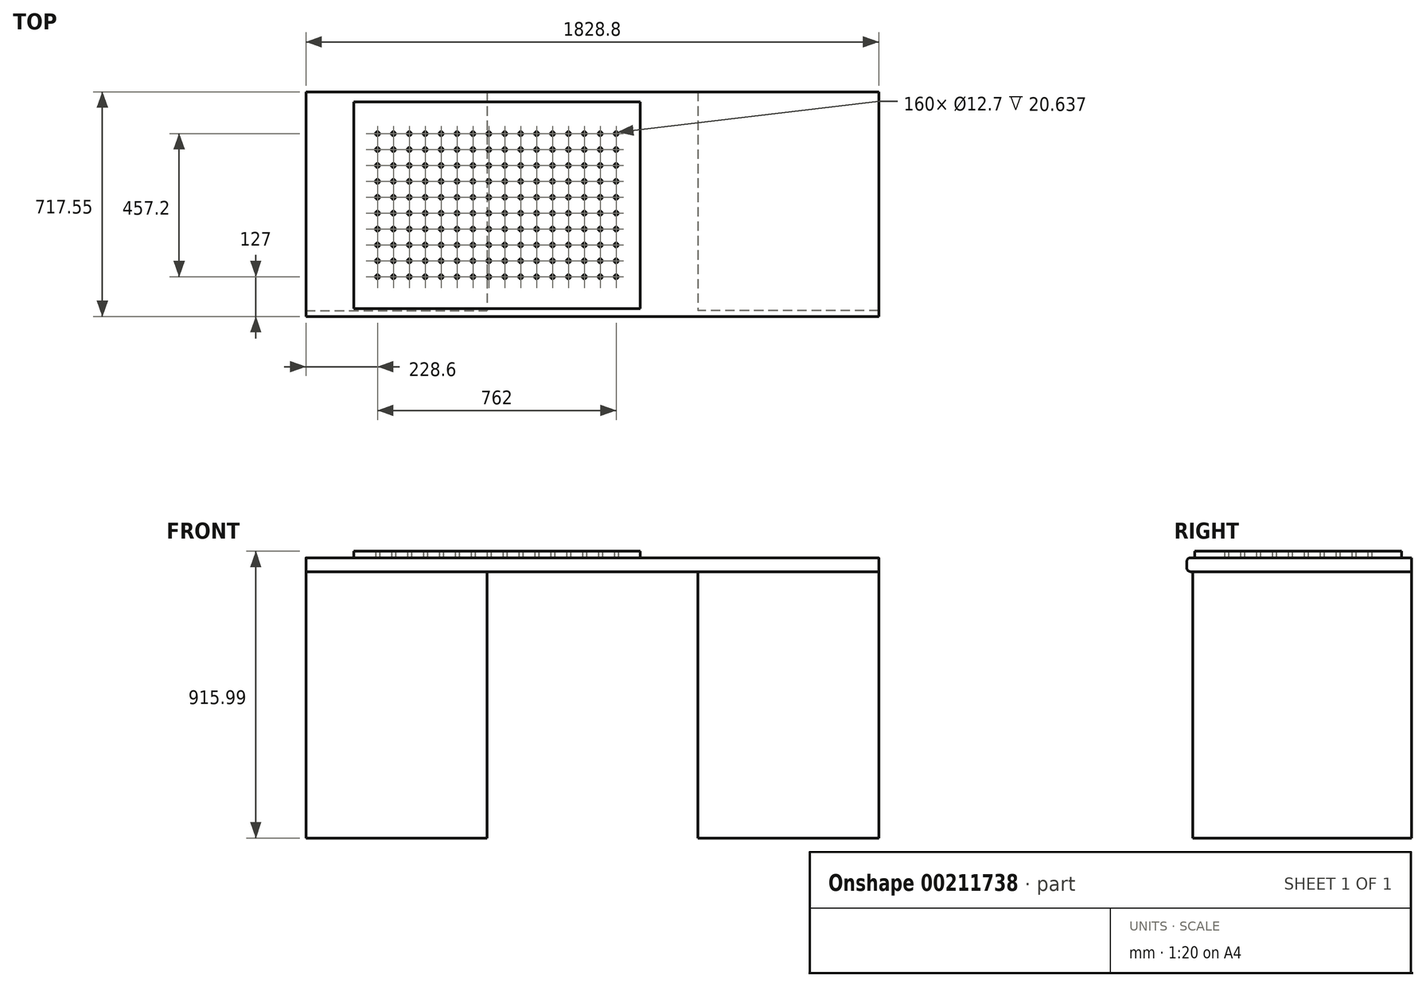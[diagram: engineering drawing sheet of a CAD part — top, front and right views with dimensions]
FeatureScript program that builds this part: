
annotation { "Feature Type Name" : "Feature", "Feature Type Description" : "" }
export const myFeature = defineFeature(function(context is Context, id is Id, definition is map)
    precondition{}
    {
        {
            var Q0;
            Q0=qCreatedBy(makeId("Top.planeOp"),FACE);
            var sketch = newSketch(context, id + "F0", { "sketchPlane" : qUnion([Q0])});
            skLineSegment(sketch, "E0.bottom", {"start": v(-914.4, 0) * mm, "end": v(-336.55, 0) * mm});
            skLineSegment(sketch, "E0.top", {"start": v(-914.4, -698.5) * mm, "end": v(-336.55, -698.5) * mm});
            skLineSegment(sketch, "E0.left", {"start": v(-914.4, 0) * mm, "end": v(-914.4, -698.5) * mm});
            skLineSegment(sketch, "E0.right", {"start": v(-336.55, 0) * mm, "end": v(-336.55, -698.5) * mm});
            skLineSegment(sketch, "E1.MirrorCS", {"start": v(914.4, 0) * mm, "end": v(336.55, 0) * mm});
            skLineSegment(sketch, "E2.MirrorCS", {"start": v(914.4, -698.5) * mm, "end": v(336.55, -698.5) * mm});
            skLineSegment(sketch, "E3.MirrorCS", {"start": v(336.55, 0) * mm, "end": v(336.55, -698.5) * mm});
            skLineSegment(sketch, "E4.MirrorCS", {"start": v(914.4, 0) * mm, "end": v(914.4, -698.5) * mm});
            skSolve(sketch);
        }
        {
            var Q0;
            Q0 = qSketchRegion(id + "F0", true);
            extrude(context, id + "F1", {"entities" : qUnion([Q0]), "depth" : 850.9 * mm});
        }
        {
            var Q0;
            Q0=makeQuery(id+"F1.opExtrude","CAP_FACE",FACE,{"disambiguationData":[OSD([sQuery(id+"F0.wireOp",EDGE,"E0.bottom"),sQuery(id+"F0.wireOp",EDGE,"E0.top"),sQuery(id+"F0.wireOp",EDGE,"E0.left"),sQuery(id+"F0.wireOp",EDGE,"E0.right")])],"isStart":false});
            var sketch = newSketch(context, id + "F2", { "sketchPlane" : qUnion([Q0])});
            skLineSegment(sketch, "E5.bottom", {"start": v(-914.4, 0) * mm, "end": v(914.4, 0) * mm});
            skLineSegment(sketch, "E5.top", {"start": v(-914.4, -717.55) * mm, "end": v(914.4, -717.55) * mm});
            skLineSegment(sketch, "E5.left", {"start": v(-914.4, 0) * mm, "end": v(-914.4, -717.55) * mm});
            skLineSegment(sketch, "E5.right", {"start": v(914.4, 0) * mm, "end": v(914.4, -717.55) * mm});
            skSolve(sketch);
        }
        {
            var Q0;
            Q0 = qSketchRegion(id + "F2", true);
            extrude(context, id + "F3", {"entities" : qUnion([Q0]), "depth" : 44.45 * mm});
        }
        {
            var Q0;
            Q0=makeQuery(id+"F3.opExtrude","CAP_FACE",FACE,{"disambiguationData":[OSD([sQuery(id+"F2.wireOp",EDGE,"E5.bottom"),sQuery(id+"F2.wireOp",EDGE,"E5.top"),sQuery(id+"F2.wireOp",EDGE,"E5.left"),sQuery(id+"F2.wireOp",EDGE,"E5.right")])],"isStart":false});
            var sketch = newSketch(context, id + "F4", { "sketchPlane" : qUnion([Q0])});
            skLineSegment(sketch, "E6.bottom", {"start": v(-762, -31.75) * mm, "end": v(152.4, -31.75) * mm});
            skLineSegment(sketch, "E6.top", {"start": v(-762, -692.15) * mm, "end": v(152.4, -692.15) * mm});
            skLineSegment(sketch, "E6.left", {"start": v(-762, -31.75) * mm, "end": v(-762, -692.15) * mm});
            skLineSegment(sketch, "E6.right", {"start": v(152.4, -31.75) * mm, "end": v(152.4, -692.15) * mm});
            skCircle(sketch, "E7", {"center": v(-685.8, -133.35) * mm, "radius": 6.35 * mm});
            skCircle(sketch, "E8.0.1.0", {"center": v(-685.8, -184.15) * mm, "radius": 6.35 * mm});
            skCircle(sketch, "E8.0.2.0", {"center": v(-685.8, -234.95) * mm, "radius": 6.35 * mm});
            skCircle(sketch, "E8.0.3.0", {"center": v(-685.8, -285.75) * mm, "radius": 6.35 * mm});
            skCircle(sketch, "E8.0.4.0", {"center": v(-685.8, -336.55) * mm, "radius": 6.35 * mm});
            skCircle(sketch, "E8.0.5.0", {"center": v(-685.8, -387.35) * mm, "radius": 6.35 * mm});
            skCircle(sketch, "E8.0.6.0", {"center": v(-685.8, -438.15) * mm, "radius": 6.35 * mm});
            skCircle(sketch, "E8.0.7.0", {"center": v(-685.8, -488.95) * mm, "radius": 6.35 * mm});
            skCircle(sketch, "E8.0.8.0", {"center": v(-685.8, -539.75) * mm, "radius": 6.35 * mm});
            skCircle(sketch, "E8.0.9.0", {"center": v(-685.8, -590.55) * mm, "radius": 6.35 * mm});
            skCircle(sketch, "E8.1.0.0", {"center": v(-635, -133.35) * mm, "radius": 6.35 * mm});
            skCircle(sketch, "E8.1.1.0", {"center": v(-635, -184.15) * mm, "radius": 6.35 * mm});
            skCircle(sketch, "E8.1.2.0", {"center": v(-635, -234.95) * mm, "radius": 6.35 * mm});
            skCircle(sketch, "E8.1.3.0", {"center": v(-635, -285.75) * mm, "radius": 6.35 * mm});
            skCircle(sketch, "E8.1.4.0", {"center": v(-635, -336.55) * mm, "radius": 6.35 * mm});
            skCircle(sketch, "E8.1.5.0", {"center": v(-635, -387.35) * mm, "radius": 6.35 * mm});
            skCircle(sketch, "E8.1.6.0", {"center": v(-635, -438.15) * mm, "radius": 6.35 * mm});
            skCircle(sketch, "E8.1.7.0", {"center": v(-635, -488.95) * mm, "radius": 6.35 * mm});
            skCircle(sketch, "E8.1.8.0", {"center": v(-635, -539.75) * mm, "radius": 6.35 * mm});
            skCircle(sketch, "E8.1.9.0", {"center": v(-635, -590.55) * mm, "radius": 6.35 * mm});
            skCircle(sketch, "E8.2.0.0", {"center": v(-584.2, -133.35) * mm, "radius": 6.35 * mm});
            skCircle(sketch, "E8.2.1.0", {"center": v(-584.2, -184.15) * mm, "radius": 6.35 * mm});
            skCircle(sketch, "E8.2.2.0", {"center": v(-584.2, -234.95) * mm, "radius": 6.35 * mm});
            skCircle(sketch, "E8.2.3.0", {"center": v(-584.2, -285.75) * mm, "radius": 6.35 * mm});
            skCircle(sketch, "E8.2.4.0", {"center": v(-584.2, -336.55) * mm, "radius": 6.35 * mm});
            skCircle(sketch, "E8.2.5.0", {"center": v(-584.2, -387.35) * mm, "radius": 6.35 * mm});
            skCircle(sketch, "E8.2.6.0", {"center": v(-584.2, -438.15) * mm, "radius": 6.35 * mm});
            skCircle(sketch, "E8.2.7.0", {"center": v(-584.2, -488.95) * mm, "radius": 6.35 * mm});
            skCircle(sketch, "E8.2.8.0", {"center": v(-584.2, -539.75) * mm, "radius": 6.35 * mm});
            skCircle(sketch, "E8.2.9.0", {"center": v(-584.2, -590.55) * mm, "radius": 6.35 * mm});
            skCircle(sketch, "E8.3.0.0", {"center": v(-533.4, -133.35) * mm, "radius": 6.35 * mm});
            skCircle(sketch, "E8.3.1.0", {"center": v(-533.4, -184.15) * mm, "radius": 6.35 * mm});
            skCircle(sketch, "E8.3.2.0", {"center": v(-533.4, -234.95) * mm, "radius": 6.35 * mm});
            skCircle(sketch, "E8.3.3.0", {"center": v(-533.4, -285.75) * mm, "radius": 6.35 * mm});
            skCircle(sketch, "E8.3.4.0", {"center": v(-533.4, -336.55) * mm, "radius": 6.35 * mm});
            skCircle(sketch, "E8.3.5.0", {"center": v(-533.4, -387.35) * mm, "radius": 6.35 * mm});
            skCircle(sketch, "E8.3.6.0", {"center": v(-533.4, -438.15) * mm, "radius": 6.35 * mm});
            skCircle(sketch, "E8.3.7.0", {"center": v(-533.4, -488.95) * mm, "radius": 6.35 * mm});
            skCircle(sketch, "E8.3.8.0", {"center": v(-533.4, -539.75) * mm, "radius": 6.35 * mm});
            skCircle(sketch, "E8.3.9.0", {"center": v(-533.4, -590.55) * mm, "radius": 6.35 * mm});
            skCircle(sketch, "E8.4.0.0", {"center": v(-482.6, -133.35) * mm, "radius": 6.35 * mm});
            skCircle(sketch, "E8.4.1.0", {"center": v(-482.6, -184.15) * mm, "radius": 6.35 * mm});
            skCircle(sketch, "E8.4.2.0", {"center": v(-482.6, -234.95) * mm, "radius": 6.35 * mm});
            skCircle(sketch, "E8.4.3.0", {"center": v(-482.6, -285.75) * mm, "radius": 6.35 * mm});
            skCircle(sketch, "E8.4.4.0", {"center": v(-482.6, -336.55) * mm, "radius": 6.35 * mm});
            skCircle(sketch, "E8.4.5.0", {"center": v(-482.6, -387.35) * mm, "radius": 6.35 * mm});
            skCircle(sketch, "E8.4.6.0", {"center": v(-482.6, -438.15) * mm, "radius": 6.35 * mm});
            skCircle(sketch, "E8.4.7.0", {"center": v(-482.6, -488.95) * mm, "radius": 6.35 * mm});
            skCircle(sketch, "E8.4.8.0", {"center": v(-482.6, -539.75) * mm, "radius": 6.35 * mm});
            skCircle(sketch, "E8.4.9.0", {"center": v(-482.6, -590.55) * mm, "radius": 6.35 * mm});
            skCircle(sketch, "E8.5.0.0", {"center": v(-431.8, -133.35) * mm, "radius": 6.35 * mm});
            skCircle(sketch, "E8.5.1.0", {"center": v(-431.8, -184.15) * mm, "radius": 6.35 * mm});
            skCircle(sketch, "E8.5.2.0", {"center": v(-431.8, -234.95) * mm, "radius": 6.35 * mm});
            skCircle(sketch, "E8.5.3.0", {"center": v(-431.8, -285.75) * mm, "radius": 6.35 * mm});
            skCircle(sketch, "E8.5.4.0", {"center": v(-431.8, -336.55) * mm, "radius": 6.35 * mm});
            skCircle(sketch, "E8.5.5.0", {"center": v(-431.8, -387.35) * mm, "radius": 6.35 * mm});
            skCircle(sketch, "E8.5.6.0", {"center": v(-431.8, -438.15) * mm, "radius": 6.35 * mm});
            skCircle(sketch, "E8.5.7.0", {"center": v(-431.8, -488.95) * mm, "radius": 6.35 * mm});
            skCircle(sketch, "E8.5.8.0", {"center": v(-431.8, -539.75) * mm, "radius": 6.35 * mm});
            skCircle(sketch, "E8.5.9.0", {"center": v(-431.8, -590.55) * mm, "radius": 6.35 * mm});
            skCircle(sketch, "E8.6.0.0", {"center": v(-381, -133.35) * mm, "radius": 6.35 * mm});
            skCircle(sketch, "E8.6.1.0", {"center": v(-381, -184.15) * mm, "radius": 6.35 * mm});
            skCircle(sketch, "E8.6.2.0", {"center": v(-381, -234.95) * mm, "radius": 6.35 * mm});
            skCircle(sketch, "E8.6.3.0", {"center": v(-381, -285.75) * mm, "radius": 6.35 * mm});
            skCircle(sketch, "E8.6.4.0", {"center": v(-381, -336.55) * mm, "radius": 6.35 * mm});
            skCircle(sketch, "E8.6.5.0", {"center": v(-381, -387.35) * mm, "radius": 6.35 * mm});
            skCircle(sketch, "E8.6.6.0", {"center": v(-381, -438.15) * mm, "radius": 6.35 * mm});
            skCircle(sketch, "E8.6.7.0", {"center": v(-381, -488.95) * mm, "radius": 6.35 * mm});
            skCircle(sketch, "E8.6.8.0", {"center": v(-381, -539.75) * mm, "radius": 6.35 * mm});
            skCircle(sketch, "E8.6.9.0", {"center": v(-381, -590.55) * mm, "radius": 6.35 * mm});
            skCircle(sketch, "E8.7.0.0", {"center": v(-330.2, -133.35) * mm, "radius": 6.35 * mm});
            skCircle(sketch, "E8.7.1.0", {"center": v(-330.2, -184.15) * mm, "radius": 6.35 * mm});
            skCircle(sketch, "E8.7.2.0", {"center": v(-330.2, -234.95) * mm, "radius": 6.35 * mm});
            skCircle(sketch, "E8.7.3.0", {"center": v(-330.2, -285.75) * mm, "radius": 6.35 * mm});
            skCircle(sketch, "E8.7.4.0", {"center": v(-330.2, -336.55) * mm, "radius": 6.35 * mm});
            skCircle(sketch, "E8.7.5.0", {"center": v(-330.2, -387.35) * mm, "radius": 6.35 * mm});
            skCircle(sketch, "E8.7.6.0", {"center": v(-330.2, -438.15) * mm, "radius": 6.35 * mm});
            skCircle(sketch, "E8.7.7.0", {"center": v(-330.2, -488.95) * mm, "radius": 6.35 * mm});
            skCircle(sketch, "E8.7.8.0", {"center": v(-330.2, -539.75) * mm, "radius": 6.35 * mm});
            skCircle(sketch, "E8.7.9.0", {"center": v(-330.2, -590.55) * mm, "radius": 6.35 * mm});
            skCircle(sketch, "E8.8.0.0", {"center": v(-279.4, -133.35) * mm, "radius": 6.35 * mm});
            skCircle(sketch, "E8.8.1.0", {"center": v(-279.4, -184.15) * mm, "radius": 6.35 * mm});
            skCircle(sketch, "E8.8.2.0", {"center": v(-279.4, -234.95) * mm, "radius": 6.35 * mm});
            skCircle(sketch, "E8.8.3.0", {"center": v(-279.4, -285.75) * mm, "radius": 6.35 * mm});
            skCircle(sketch, "E8.8.4.0", {"center": v(-279.4, -336.55) * mm, "radius": 6.35 * mm});
            skCircle(sketch, "E8.8.5.0", {"center": v(-279.4, -387.35) * mm, "radius": 6.35 * mm});
            skCircle(sketch, "E8.8.6.0", {"center": v(-279.4, -438.15) * mm, "radius": 6.35 * mm});
            skCircle(sketch, "E8.8.7.0", {"center": v(-279.4, -488.95) * mm, "radius": 6.35 * mm});
            skCircle(sketch, "E8.8.8.0", {"center": v(-279.4, -539.75) * mm, "radius": 6.35 * mm});
            skCircle(sketch, "E8.8.9.0", {"center": v(-279.4, -590.55) * mm, "radius": 6.35 * mm});
            skCircle(sketch, "E8.9.0.0", {"center": v(-228.6, -133.35) * mm, "radius": 6.35 * mm});
            skCircle(sketch, "E8.9.1.0", {"center": v(-228.6, -184.15) * mm, "radius": 6.35 * mm});
            skCircle(sketch, "E8.9.2.0", {"center": v(-228.6, -234.95) * mm, "radius": 6.35 * mm});
            skCircle(sketch, "E8.9.3.0", {"center": v(-228.6, -285.75) * mm, "radius": 6.35 * mm});
            skCircle(sketch, "E8.9.4.0", {"center": v(-228.6, -336.55) * mm, "radius": 6.35 * mm});
            skCircle(sketch, "E8.9.5.0", {"center": v(-228.6, -387.35) * mm, "radius": 6.35 * mm});
            skCircle(sketch, "E8.9.6.0", {"center": v(-228.6, -438.15) * mm, "radius": 6.35 * mm});
            skCircle(sketch, "E8.9.7.0", {"center": v(-228.6, -488.95) * mm, "radius": 6.35 * mm});
            skCircle(sketch, "E8.9.8.0", {"center": v(-228.6, -539.75) * mm, "radius": 6.35 * mm});
            skCircle(sketch, "E8.9.9.0", {"center": v(-228.6, -590.55) * mm, "radius": 6.35 * mm});
            skCircle(sketch, "E8.10.0.0", {"center": v(-177.8, -133.35) * mm, "radius": 6.35 * mm});
            skCircle(sketch, "E8.10.1.0", {"center": v(-177.8, -184.15) * mm, "radius": 6.35 * mm});
            skCircle(sketch, "E8.10.2.0", {"center": v(-177.8, -234.95) * mm, "radius": 6.35 * mm});
            skCircle(sketch, "E8.10.3.0", {"center": v(-177.8, -285.75) * mm, "radius": 6.35 * mm});
            skCircle(sketch, "E8.10.4.0", {"center": v(-177.8, -336.55) * mm, "radius": 6.35 * mm});
            skCircle(sketch, "E8.10.5.0", {"center": v(-177.8, -387.35) * mm, "radius": 6.35 * mm});
            skCircle(sketch, "E8.10.6.0", {"center": v(-177.8, -438.15) * mm, "radius": 6.35 * mm});
            skCircle(sketch, "E8.10.7.0", {"center": v(-177.8, -488.95) * mm, "radius": 6.35 * mm});
            skCircle(sketch, "E8.10.8.0", {"center": v(-177.8, -539.75) * mm, "radius": 6.35 * mm});
            skCircle(sketch, "E8.10.9.0", {"center": v(-177.8, -590.55) * mm, "radius": 6.35 * mm});
            skCircle(sketch, "E8.11.0.0", {"center": v(-127, -133.35) * mm, "radius": 6.35 * mm});
            skCircle(sketch, "E8.11.1.0", {"center": v(-127, -184.15) * mm, "radius": 6.35 * mm});
            skCircle(sketch, "E8.11.2.0", {"center": v(-127, -234.95) * mm, "radius": 6.35 * mm});
            skCircle(sketch, "E8.11.3.0", {"center": v(-127, -285.75) * mm, "radius": 6.35 * mm});
            skCircle(sketch, "E8.11.4.0", {"center": v(-127, -336.55) * mm, "radius": 6.35 * mm});
            skCircle(sketch, "E8.11.5.0", {"center": v(-127, -387.35) * mm, "radius": 6.35 * mm});
            skCircle(sketch, "E8.11.6.0", {"center": v(-127, -438.15) * mm, "radius": 6.35 * mm});
            skCircle(sketch, "E8.11.7.0", {"center": v(-127, -488.95) * mm, "radius": 6.35 * mm});
            skCircle(sketch, "E8.11.8.0", {"center": v(-127, -539.75) * mm, "radius": 6.35 * mm});
            skCircle(sketch, "E8.11.9.0", {"center": v(-127, -590.55) * mm, "radius": 6.35 * mm});
            skCircle(sketch, "E8.12.0.0", {"center": v(-76.2, -133.35) * mm, "radius": 6.35 * mm});
            skCircle(sketch, "E8.12.1.0", {"center": v(-76.2, -184.15) * mm, "radius": 6.35 * mm});
            skCircle(sketch, "E8.12.2.0", {"center": v(-76.2, -234.95) * mm, "radius": 6.35 * mm});
            skCircle(sketch, "E8.12.3.0", {"center": v(-76.2, -285.75) * mm, "radius": 6.35 * mm});
            skCircle(sketch, "E8.12.4.0", {"center": v(-76.2, -336.55) * mm, "radius": 6.35 * mm});
            skCircle(sketch, "E8.12.5.0", {"center": v(-76.2, -387.35) * mm, "radius": 6.35 * mm});
            skCircle(sketch, "E8.12.6.0", {"center": v(-76.2, -438.15) * mm, "radius": 6.35 * mm});
            skCircle(sketch, "E8.12.7.0", {"center": v(-76.2, -488.95) * mm, "radius": 6.35 * mm});
            skCircle(sketch, "E8.12.8.0", {"center": v(-76.2, -539.75) * mm, "radius": 6.35 * mm});
            skCircle(sketch, "E8.12.9.0", {"center": v(-76.2, -590.55) * mm, "radius": 6.35 * mm});
            skCircle(sketch, "E8.13.0.0", {"center": v(-25.4, -133.35) * mm, "radius": 6.35 * mm});
            skCircle(sketch, "E8.13.1.0", {"center": v(-25.4, -184.15) * mm, "radius": 6.35 * mm});
            skCircle(sketch, "E8.13.2.0", {"center": v(-25.4, -234.95) * mm, "radius": 6.35 * mm});
            skCircle(sketch, "E8.13.3.0", {"center": v(-25.4, -285.75) * mm, "radius": 6.35 * mm});
            skCircle(sketch, "E8.13.4.0", {"center": v(-25.4, -336.55) * mm, "radius": 6.35 * mm});
            skCircle(sketch, "E8.13.5.0", {"center": v(-25.4, -387.35) * mm, "radius": 6.35 * mm});
            skCircle(sketch, "E8.13.6.0", {"center": v(-25.4, -438.15) * mm, "radius": 6.35 * mm});
            skCircle(sketch, "E8.13.7.0", {"center": v(-25.4, -488.95) * mm, "radius": 6.35 * mm});
            skCircle(sketch, "E8.13.8.0", {"center": v(-25.4, -539.75) * mm, "radius": 6.35 * mm});
            skCircle(sketch, "E8.13.9.0", {"center": v(-25.4, -590.55) * mm, "radius": 6.35 * mm});
            skCircle(sketch, "E8.14.0.0", {"center": v(25.4, -133.35) * mm, "radius": 6.35 * mm});
            skCircle(sketch, "E8.14.1.0", {"center": v(25.4, -184.15) * mm, "radius": 6.35 * mm});
            skCircle(sketch, "E8.14.2.0", {"center": v(25.4, -234.95) * mm, "radius": 6.35 * mm});
            skCircle(sketch, "E8.14.3.0", {"center": v(25.4, -285.75) * mm, "radius": 6.35 * mm});
            skCircle(sketch, "E8.14.4.0", {"center": v(25.4, -336.55) * mm, "radius": 6.35 * mm});
            skCircle(sketch, "E8.14.5.0", {"center": v(25.4, -387.35) * mm, "radius": 6.35 * mm});
            skCircle(sketch, "E8.14.6.0", {"center": v(25.4, -438.15) * mm, "radius": 6.35 * mm});
            skCircle(sketch, "E8.14.7.0", {"center": v(25.4, -488.95) * mm, "radius": 6.35 * mm});
            skCircle(sketch, "E8.14.8.0", {"center": v(25.4, -539.75) * mm, "radius": 6.35 * mm});
            skCircle(sketch, "E8.14.9.0", {"center": v(25.4, -590.55) * mm, "radius": 6.35 * mm});
            skCircle(sketch, "E8.15.0.0", {"center": v(76.2, -133.35) * mm, "radius": 6.35 * mm});
            skCircle(sketch, "E8.15.1.0", {"center": v(76.2, -184.15) * mm, "radius": 6.35 * mm});
            skCircle(sketch, "E8.15.2.0", {"center": v(76.2, -234.95) * mm, "radius": 6.35 * mm});
            skCircle(sketch, "E8.15.3.0", {"center": v(76.2, -285.75) * mm, "radius": 6.35 * mm});
            skCircle(sketch, "E8.15.4.0", {"center": v(76.2, -336.55) * mm, "radius": 6.35 * mm});
            skCircle(sketch, "E8.15.5.0", {"center": v(76.2, -387.35) * mm, "radius": 6.35 * mm});
            skCircle(sketch, "E8.15.6.0", {"center": v(76.2, -438.15) * mm, "radius": 6.35 * mm});
            skCircle(sketch, "E8.15.7.0", {"center": v(76.2, -488.95) * mm, "radius": 6.35 * mm});
            skCircle(sketch, "E8.15.8.0", {"center": v(76.2, -539.75) * mm, "radius": 6.35 * mm});
            skCircle(sketch, "E8.15.9.0", {"center": v(76.2, -590.55) * mm, "radius": 6.35 * mm});
            skLineSegment(sketch, "E8.direction1", {"start": v(-685.8, -133.35) * mm, "end": v(-635, -133.35) * mm, "construction": true});
            skLineSegment(sketch, "E8.direction2", {"start": v(-685.8, -133.35) * mm, "end": v(-685.8, -184.15) * mm, "construction": true});
            skSolve(sketch);
        }
        {
            var Q0;
            Q0 = qSketchRegion(id + "F4", true);
            extrude(context, id + "F5", {"entities" : qUnion([Q0]), "operationType" : NewBodyOperationType.ADD, "depth" : 20.64 * mm});
        }
        {
            var Q0;
            Q0=makeQuery(id+"F3.opExtrude","CAP_EDGE",EDGE,{"disambiguationData":[OSD([sQuery(id+"F2.wireOp",EDGE,"E5.top")])],"isStart":false});
            var Q1;
            Q1=makeQuery(id+"F3.opExtrude","CAP_EDGE",EDGE,{"disambiguationData":[OSD([sQuery(id+"F2.wireOp",EDGE,"E5.top")])],"isStart":true});
            fillet(context, id + "F6", {"entities" : qUnion([Q0, Q1]), "radius" : 12.7 * mm, "tangentPropagation" : true, "allowEdgeOverflow" : false});
        }
    });
